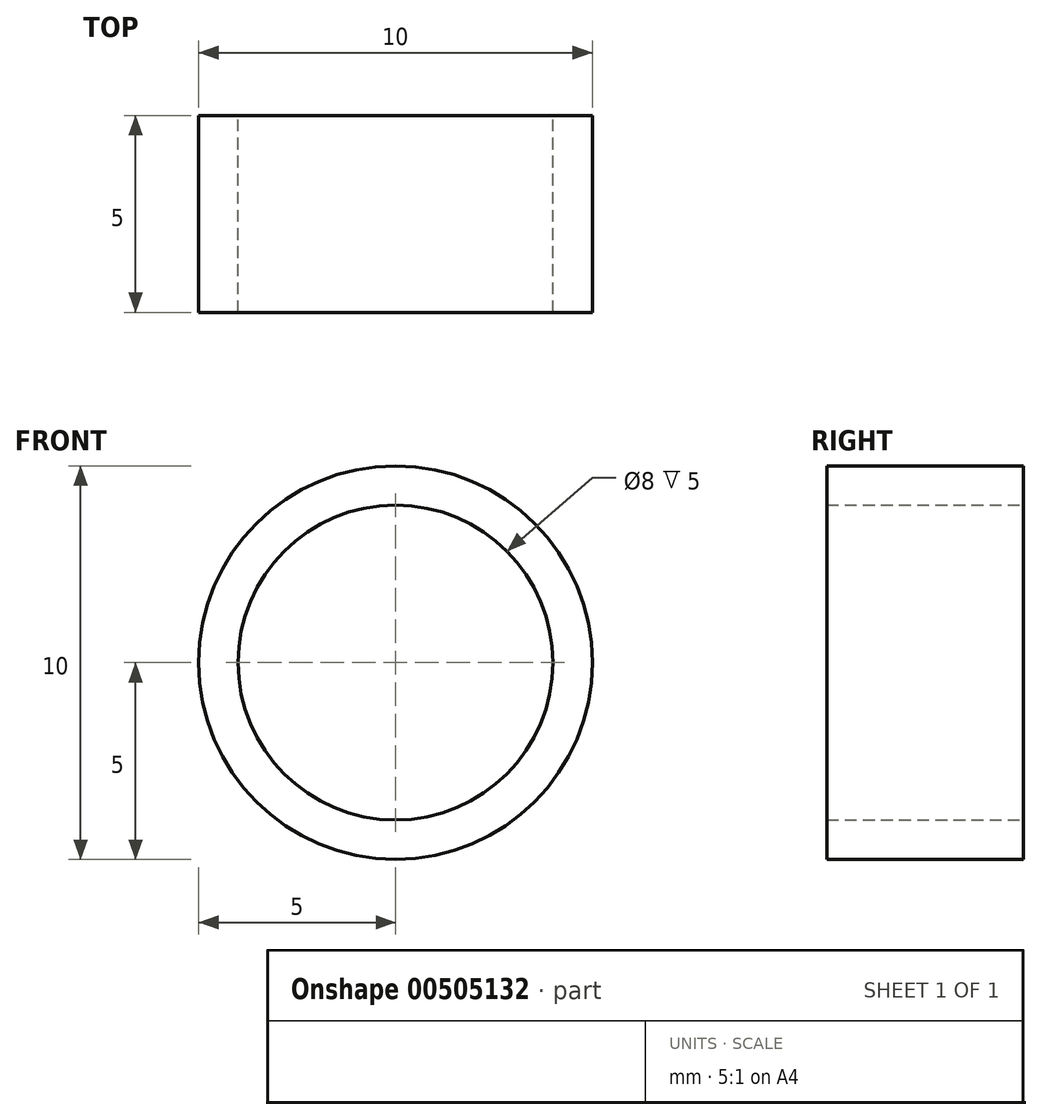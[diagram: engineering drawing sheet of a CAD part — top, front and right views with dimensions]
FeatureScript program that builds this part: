
annotation { "Feature Type Name" : "Feature", "Feature Type Description" : "" }
export const myFeature = defineFeature(function(context is Context, id is Id, definition is map)
    precondition{}
    {
        {
            var Q0;
            Q0=qCreatedBy(makeId("Front.planeOp"),FACE);
            var sketch = newSketch(context, id + "F0", { "sketchPlane" : qUnion([Q0])});
            skCircle(sketch, "E0", {"center": v(0, 0) * mm, "radius": 5 * mm});
            skSolve(sketch);
        }
        {
            var Q0;
            Q0=makeQuery(id+"F0.imprint","IMPRINT",FACE,{"disambiguationData":[TD([[makeQuery(id+"F0.imprint","IMPRINT",EDGE,{"derivedFrom":sQuery(id+"F0.wireOp",EDGE,"E0")}),1.0]])]});
            extrude(context, id + "F1", {"entities" : qUnion([Q0]), "depth" : 5 * mm, "offsetDistance" : 25 * mm});
        }
        {
            var Q0;
            Q0=qCreatedBy(makeId("Front.planeOp"),FACE);
            var sketch = newSketch(context, id + "F2", { "sketchPlane" : qUnion([Q0])});
            skCircle(sketch, "E1", {"center": v(0, 0) * mm, "radius": 4 * mm});
            skSolve(sketch);
        }
        {
            var Q0;
            Q0 = qSketchRegion(id + "F2", true);
            extrude(context, id + "F3", {"entities" : qUnion([Q0]), "operationType" : NewBodyOperationType.REMOVE, "depth" : 5 * mm, "offsetDistance" : 25 * mm});
        }
    });
